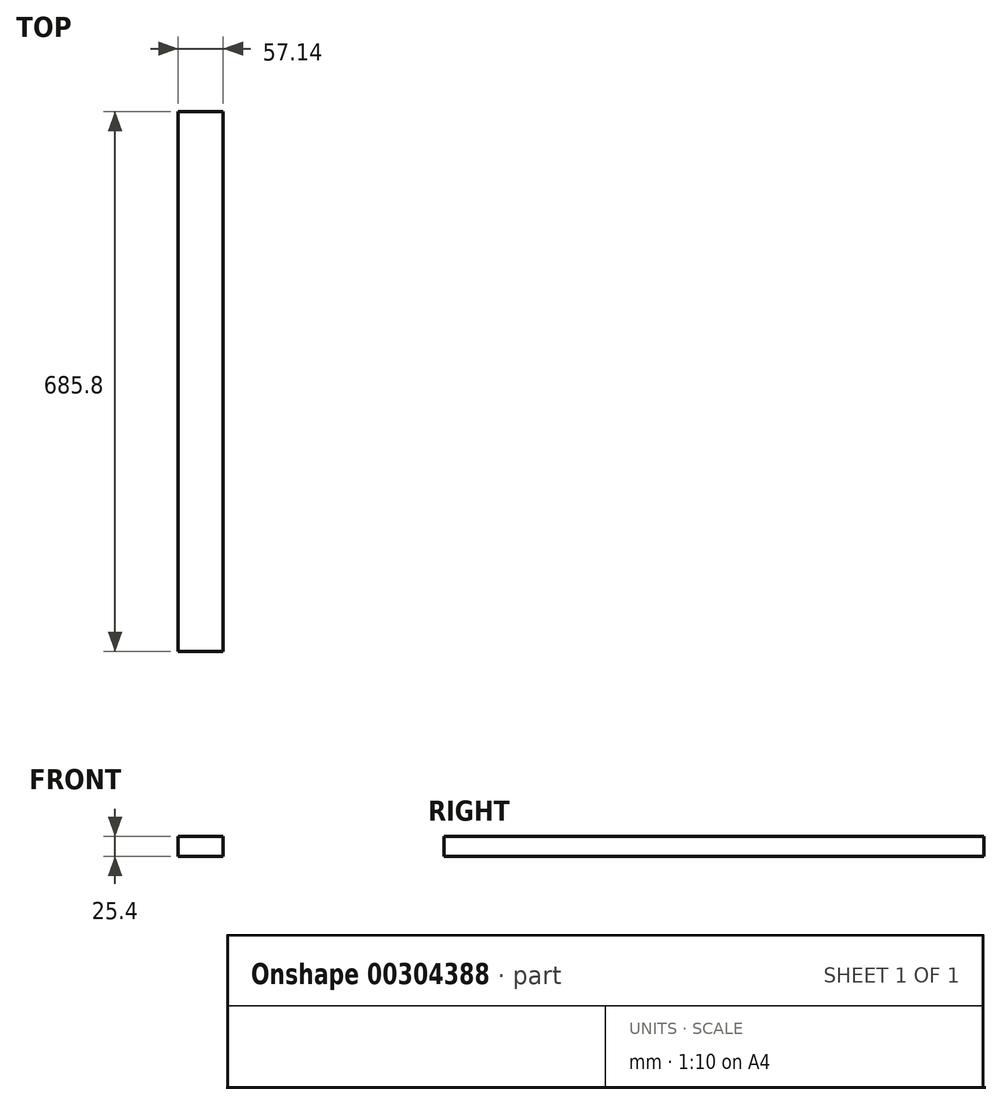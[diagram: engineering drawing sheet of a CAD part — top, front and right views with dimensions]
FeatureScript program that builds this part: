
annotation { "Feature Type Name" : "Feature", "Feature Type Description" : "" }
export const myFeature = defineFeature(function(context is Context, id is Id, definition is map)
    precondition{}
    {
        {
            var Q0;
            Q0=qCreatedBy(makeId("Top.planeOp"),FACE);
            var sketch = newSketch(context, id + "F0", { "sketchPlane" : qUnion([Q0])});
            skLineSegment(sketch, "E0.bottom", {"start": v(-28.58, 342.9) * mm, "end": v(28.57, 342.9) * mm});
            skLineSegment(sketch, "E0.top", {"start": v(-28.58, -342.9) * mm, "end": v(28.57, -342.9) * mm});
            skLineSegment(sketch, "E0.left", {"start": v(-28.58, 342.9) * mm, "end": v(-28.58, -342.9) * mm});
            skLineSegment(sketch, "E0.right", {"start": v(28.57, 342.9) * mm, "end": v(28.57, -342.9) * mm});
            skPoint(sketch, "E0.middle", {"position": v(0, 0) * mm});
            skSolve(sketch);
        }
        {
            var Q0;
            Q0=makeQuery(id+"F0.imprint","IMPRINT",FACE,{"disambiguationData":[TD([[makeQuery(id+"F0.imprint","IMPRINT",EDGE,{"derivedFrom":sQuery(id+"F0.wireOp",EDGE,"E0.bottom")}),-1.0]])]});
            extrude(context, id + "F1", {"entities" : qUnion([Q0]), "depth" : 25.4 * mm});
        }
    });
